# Revit family: УЗ-15
name_source: partatom
category: Арматура трубопроводов
units: mm (PartAtom-declared; Revit-internal decimal feet)

## family parameters
Всегда вертикально = Да
На основе рабочей плоскости = Нет
Общий = Нет
При загрузке вырезать с полостями = Нет
Размер круглого соединителя = Использовать диаметр
Тип детали = Клапан - Вставляется

## types (2) — shared parameters
ADSK_Единица измерения = шт.
ADSK_Завод-изготовитель = РУП "БЕЛГАЗТЕХНИКА"
ADSK_Класс герметичности по ГОСТ 9544-2005 = А
ADSK_Количество = 1
ADSK_Марка = УЗ-15
ADSK_Номинальное давление, МПа, не более = 1,2
zero-valued in all types: Отметка по умолчанию

## per-type parameters (varying)
| type | ADSK_Масса_Текст | ADSK_Материал наименование | ADSK_Наименование | ADSK_Тип соединения |
| с муфтой алюминиевой | 0,26 кг | АК 12 | Устройство запорное DN15, А ТУ BY 100270876.119-2005 | резобовое G 1/2, размер под ключ 27 мм |
| с муфтой латунной | 0,4 кг | латунь | Устройство запорное DN15, Л ТУ BY 100270876.119-2005 | резьбовое G 1/2, размер под ключ 27 мм |
